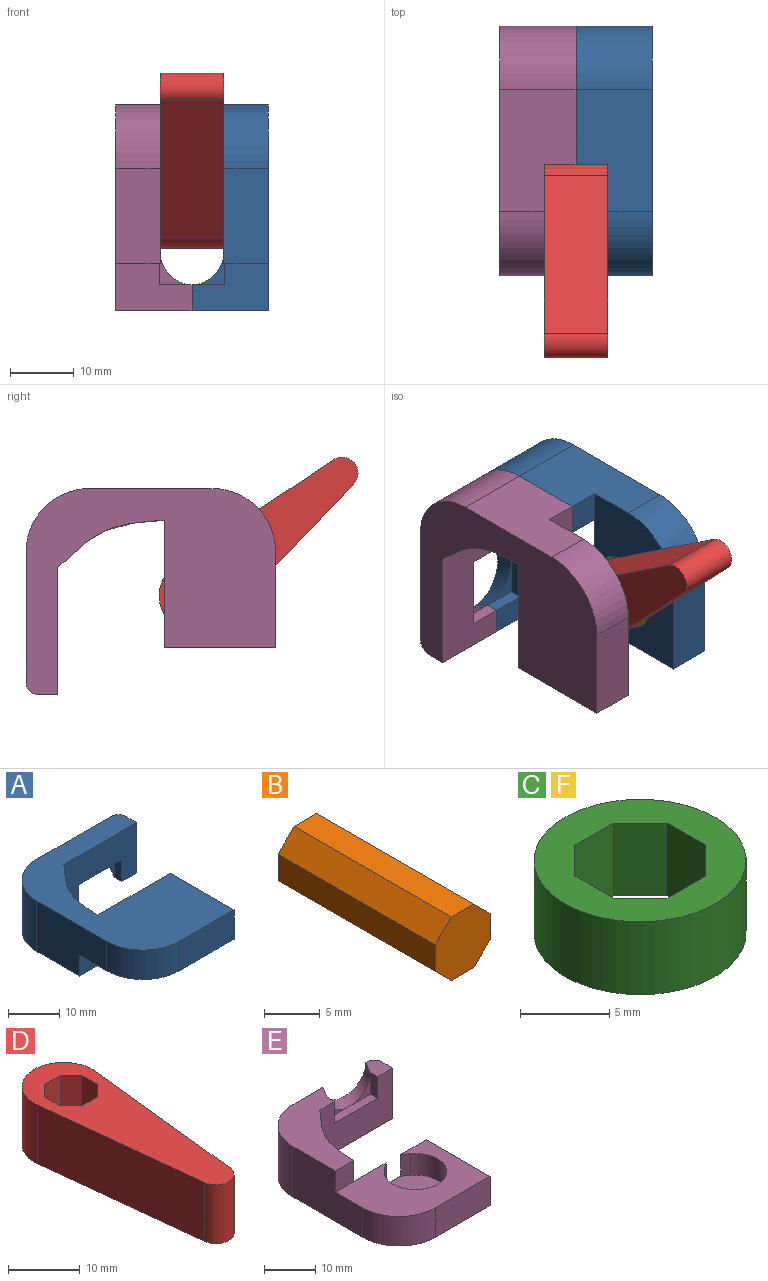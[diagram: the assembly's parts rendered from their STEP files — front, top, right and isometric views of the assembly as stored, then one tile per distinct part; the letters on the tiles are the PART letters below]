
ASSEMBLY  parts=6 mates=5
PART A: 26 faces, bbox 32.4x39.2x12 mm
  f0: plane 5.92x5.15mm, normal (0,-1,0), area 6.5mm2, adj f21,f22,f25
  f1: plane 21.7x18.2mm, normal (0,0,-1), area 183.2mm2, adj f2,f4,f9,f12,f13,f19,f24,f25
  f2: plane 20x12mm, normal (0,-1,0), area 179mm2, adj f1,f9,f10,f14,f20,f21,f22,f24
  f3: plane 25x17.5mm, normal (0,0,-1), area 298.3mm2, adj f4,f5,f6,f7,f8,f15,f16,f17
  f4: plane 19.2x12mm, normal (-1,0,0), area 192.9mm2, adj f1,f3,f5,f13,f14,f19
  f5: cylinder r=10mm len=10mm, axis (0,0,1), area 110mm2, adj f3,f4,f6,f14
  f6: plane 15x7mm, normal (0,-1,0), area 105mm2, adj f3,f5,f7,f14
  f7: plane 17.5x7mm, normal (1,0,0), area 122.5mm2, adj f3,f6,f8,f14
  f8: plane 20x7mm, normal (0,1,0), area 119.4mm2, adj f3,f7,f9,f14,f15,f16,f18
  f9: extruded ~16.7x12mm, area 226.9mm2, adj f1,f2,f8,f14,f19
  f10: plane 12x3mm, normal (1,0,0), area 36mm2, adj f2,f11,f14,f20
  f11: cylinder r=2mm len=12mm, axis (0,0,1), area 37.7mm2, adj f10,f12,f14,f20
  f12: plane 20.4x12mm, normal (0,1,0), area 196.8mm2, adj f1,f11,f13,f14,f20,f25
  f13: cylinder r=10mm len=12mm, axis (0,0,1), area 188.5mm2, adj f1,f4,f12,f14
  f14: plane 39.2x32.4mm, normal (0,0,1), area 675.4mm2, adj f2,f4,f5,f6,f7,f8,f9,f10
  f15: plane 5.15x1.61mm, normal (-0.59,-0.81,0), area 10.3mm2, adj f3,f8,f17,f18
  f16: plane 5.15x1.61mm, normal (0.59,-0.81,0), area 10.3mm2, adj f3,f8,f17,f18
  f17: cylinder r=6.1mm len=12.2mm, axis (0,0,-1), area 157.6mm2, adj f3,f15,f16,f18
  f18: plane 12.2x12.2mm, normal (0,0,-1), area 117.7mm2, adj f8,f15,f16,f17
  f19: plane 5x5mm, normal (0,-1,0), area 25mm2, adj f1,f3,f4,f9
  f20: plane 5x4.08mm, normal (0,0,-1), area 16.9mm2, adj f2,f10,f11,f12,f22,f25
  f21: plane 11.85x2mm, normal (0,0,-1), area 23.7mm2, adj f0,f2,f22,f23,f24
  f22: plane 5.15x2mm, normal (-1,0,0), area 10.3mm2, adj f0,f2,f20,f21
  f23: plane 5.92x5.15mm, normal (0,-1,0), area 6.5mm2, adj f21,f24,f25
  f24: plane 5.15x2mm, normal (1,0,0), area 10.3mm2, adj f1,f2,f21,f23
  f25: bspline ~13.58x10.3mm, area 55.9mm2, adj f0,f1,f12,f20,f23
PART B: 10 faces, bbox 7x20x7 mm
  f0: plane 20x2.05mm, normal (0.71,0,0.71), area 58mm2, adj f1,f7,f8,f9
  f1: plane 20x2.9mm, normal (0,0,1), area 58mm2, adj f0,f2,f8,f9
  f2: plane 20x2.05mm, normal (-0.71,0,0.71), area 58mm2, adj f1,f3,f8,f9
  f3: plane 20x2.9mm, normal (-1,0,0), area 58mm2, adj f2,f4,f8,f9
  f4: plane 20x2.05mm, normal (-0.71,0,-0.71), area 58mm2, adj f3,f5,f8,f9
  f5: plane 20x2.9mm, normal (0,0,-1), area 58mm2, adj f4,f6,f8,f9
  f6: plane 20x2.05mm, normal (0.71,0,-0.71), area 58mm2, adj f5,f7,f8,f9
  f7: plane 20x2.9mm, normal (1,0,0), area 58mm2, adj f0,f6,f8,f9
  f8: plane 7x7mm, normal (0,-1,0), area 40.6mm2, adj f0,f1,f2,f3,f4,f5,f6,f7
  f9: plane 7x7mm, normal (0,1,0), area 40.6mm2, adj f0,f1,f2,f3,f4,f5,f6,f7
PART C: 11 faces, bbox 11.9x11.9x5 mm
  f0: plane 5x3.02mm, normal (0,-1,0), area 15.1mm2, adj f1,f7,f9,f10
  f1: plane 5x2.14mm, normal (-0.71,-0.71,0), area 15.1mm2, adj f0,f2,f9,f10
  f2: plane 5x3.02mm, normal (-1,0,0), area 15.1mm2, adj f1,f3,f9,f10
  f3: plane 5x2.14mm, normal (-0.71,0.71,0), area 15.1mm2, adj f2,f4,f9,f10
  f4: plane 5x3.02mm, normal (0,1,0), area 15.1mm2, adj f3,f5,f9,f10
  f5: plane 5x2.14mm, normal (0.71,0.71,0), area 15.1mm2, adj f4,f6,f9,f10
  f6: plane 5x3.02mm, normal (1,0,0), area 15.1mm2, adj f5,f7,f9,f10
  f7: plane 5x2.14mm, normal (0.71,-0.71,0), area 15.1mm2, adj f0,f6,f9,f10
  f8: cylinder r=5.95mm len=11.9mm, axis (0,0,-1), area 186.9mm2, adj f9,f10
  f9: plane 11.9x11.9mm, normal (0,0,1), area 67.1mm2, adj f0,f1,f2,f3,f4,f5,f6,f7
  f10: plane 11.9x11.9mm, normal (0,0,-1), area 67.1mm2, adj f0,f1,f2,f3,f4,f5,f6,f7
PART D: 14 faces, bbox 11.5x38.3x10 mm
  f0: plane 29.65x10mm, normal (-0.99,-0.11,0), area 298.2mm2, adj f1,f11,f12,f13
  f1: cylinder r=2.5mm len=10mm, axis (0,0,-1), area 73.1mm2, adj f0,f2,f12,f13
  f2: plane 29.65x10mm, normal (0.99,-0.11,0), area 298.2mm2, adj f1,f11,f12,f13
  f3: plane 10x3.02mm, normal (0,-1,0), area 30.2mm2, adj f4,f10,f12,f13
  f4: plane 10x2.14mm, normal (-0.71,-0.71,0), area 30.2mm2, adj f3,f5,f12,f13
  f5: plane 10x3.02mm, normal (-1,0,0), area 30.2mm2, adj f4,f6,f12,f13
  f6: plane 10x2.14mm, normal (-0.71,0.71,0), area 30.2mm2, adj f5,f7,f12,f13
  f7: plane 10x3.02mm, normal (0,1,0), area 30.2mm2, adj f6,f8,f12,f13
  f8: plane 10x2.14mm, normal (0.71,0.71,0), area 30.2mm2, adj f7,f9,f12,f13
  f9: plane 10x3.02mm, normal (1,0,0), area 30.2mm2, adj f8,f10,f12,f13
  f10: plane 10x2.14mm, normal (0.71,-0.71,0), area 30.2mm2, adj f3,f9,f12,f13
  f11: cylinder r=5.75mm len=11.5mm, axis (0,0,-1), area 193.1mm2, adj f0,f2,f12,f13
  f12: plane 38.25x11.5mm, normal (0,0,1), area 266.6mm2, adj f0,f1,f2,f3,f4,f5,f6,f7
  f13: plane 38.25x11.5mm, normal (0,0,-1), area 266.6mm2, adj f0,f1,f2,f3,f4,f5,f6,f7
PART E: 26 faces, bbox 32.4x39.2x12 mm
  f0: plane 5.92x5.15mm, normal (0,-1,0), area 6.5mm2, adj f21,f22,f25
  f1: plane 21.7x18.2mm, normal (0,0,1), area 183.2mm2, adj f2,f4,f9,f12,f13,f19,f24,f25
  f2: plane 20x12mm, normal (0,-1,0), area 179mm2, adj f1,f9,f10,f14,f20,f21,f22,f24
  f3: plane 25x17.5mm, normal (0,0,1), area 298.3mm2, adj f4,f5,f6,f7,f8,f15,f16,f17
  f4: plane 19.2x12mm, normal (-1,0,0), area 192.9mm2, adj f1,f3,f5,f13,f14,f19
  f5: cylinder r=10mm len=10mm, axis (0,0,-1), area 110mm2, adj f3,f4,f6,f14
  f6: plane 15x7mm, normal (0,-1,0), area 105mm2, adj f3,f5,f7,f14
  f7: plane 17.5x7mm, normal (1,0,0), area 122.5mm2, adj f3,f6,f8,f14
  f8: plane 20x7mm, normal (0,1,0), area 119.4mm2, adj f3,f7,f9,f14,f15,f16,f18
  f9: extruded ~16.7x12mm, area 226.9mm2, adj f1,f2,f8,f14,f19
  f10: plane 12x3mm, normal (1,0,0), area 36mm2, adj f2,f11,f14,f20
  f11: cylinder r=2mm len=12mm, axis (0,0,-1), area 37.7mm2, adj f10,f12,f14,f20
  f12: plane 20.4x12mm, normal (0,1,0), area 196.8mm2, adj f1,f11,f13,f14,f20,f25
  f13: cylinder r=10mm len=12mm, axis (0,0,-1), area 188.5mm2, adj f1,f4,f12,f14
  f14: plane 39.2x32.4mm, normal (0,0,-1), area 675.4mm2, adj f2,f4,f5,f6,f7,f8,f9,f10
  f15: plane 5.15x1.61mm, normal (-0.59,-0.81,0), area 10.3mm2, adj f3,f8,f17,f18
  f16: plane 5.15x1.61mm, normal (0.59,-0.81,0), area 10.3mm2, adj f3,f8,f17,f18
  f17: cylinder r=6.1mm len=12.2mm, axis (0,0,1), area 157.6mm2, adj f3,f15,f16,f18
  f18: plane 12.2x12.2mm, normal (0,0,1), area 117.7mm2, adj f8,f15,f16,f17
  f19: plane 5x5mm, normal (0,-1,0), area 25mm2, adj f1,f3,f4,f9
  f20: plane 5x4.08mm, normal (0,0,1), area 16.9mm2, adj f2,f10,f11,f12,f22,f25
  f21: plane 11.85x2mm, normal (0,0,1), area 23.7mm2, adj f0,f2,f22,f23,f24
  f22: plane 5.15x2mm, normal (-1,0,0), area 10.3mm2, adj f0,f2,f20,f21
  f23: plane 5.92x5.15mm, normal (0,-1,0), area 6.5mm2, adj f21,f24,f25
  f24: plane 5.15x2mm, normal (1,0,0), area 10.3mm2, adj f1,f2,f21,f23
  f25: bspline ~13.58x10.3mm, area 55.9mm2, adj f0,f1,f12,f20,f23
PART F: same geometry as C
PLACE A rot(axis=(0,1,0),90deg) t=(3.5,-16.7,7.4)mm
PLACE B rot(axis=(-0.67,0.67,0.31),145.2deg) t=(12,-22.8,16.5)mm
PLACE C rot(axis=(-0.32,0.89,-0.32),96.7deg) t=(4.5,-22.8,16.5)mm
PLACE D rot(axis=(-0.32,0.89,-0.32),96.7deg) t=(12,-22.8,16.5)mm
PLACE E rot(axis=(0,1,0),90deg) t=(3.5,-16.7,7.4)mm
PLACE F rot(axis=(-0.32,0.89,-0.32),96.7deg) t=(19.5,-22.8,16.5)mm
MATE fastened B.f8 <-> F.f8  axis (1,0,0) through (22,-22.8,16.5)mm
MATE fastened C.f8 <-> B.f9  axis (-1,0,0) through (2,-22.8,16.5)mm
MATE fastened A.f20 <-> E.f20  axis (-1,0,0) through (12,2.17,1.89)mm
MATE revolute C.f8 <-> E.f17  axis (-1,0,0) through (2,-22.8,16.5)mm
MATE fastened D.f12 <-> F.f10  axis (1,0,0) through (17,-20.45,19.29)mm
